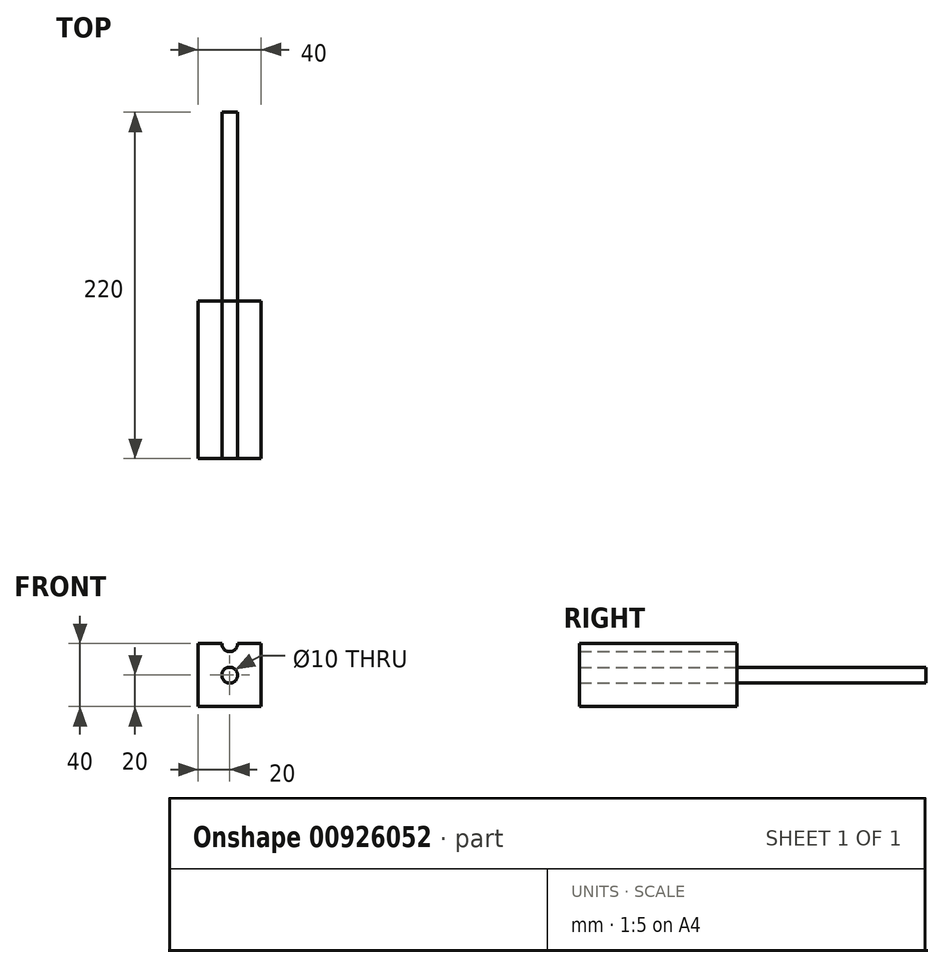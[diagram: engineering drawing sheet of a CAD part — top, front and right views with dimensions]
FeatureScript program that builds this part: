
annotation { "Feature Type Name" : "Feature", "Feature Type Description" : "" }
export const myFeature = defineFeature(function(context is Context, id is Id, definition is map)
    precondition{}
    {
        {
            var Q0;
            Q0=qCreatedBy(makeId("Front.planeOp"),FACE);
            var sketch = newSketch(context, id + "F0", { "sketchPlane" : qUnion([Q0])});
            skLineSegment(sketch, "E0.bottom", {"start": v(-20, 20) * mm, "end": v(-5, 20) * mm});
            skLineSegment(sketch, "E0.top", {"start": v(-20, -20) * mm, "end": v(20, -20) * mm});
            skLineSegment(sketch, "E0.left", {"start": v(-20, 20) * mm, "end": v(-20, -20) * mm});
            skLineSegment(sketch, "E0.right", {"start": v(20, 20) * mm, "end": v(20, -20) * mm});
            skArc(sketch, "E1", {"start": v(-5, 20) * mm, "mid": v(0, 15) * mm, "end": v(5, 20) * mm});
            skLineSegment(sketch, "E2.trimOffspring", {"start": v(5, 20) * mm, "end": v(20, 20) * mm});
            skCircle(sketch, "E3", {"center": v(0, 0) * mm, "radius": 5 * mm});
            skSolve(sketch);
        }
        {
            var Q0;
            Q0 = qSketchRegion(id + "F0", true);
            extrude(context, id + "F1", {"entities" : qUnion([Q0]), "depth" : 100 * mm, "offsetDistance" : 25.4 * mm});
        }
        {
            var Q0;
            Q0=qCreatedBy(makeId("Front.planeOp"),FACE);
            var sketch = newSketch(context, id + "F2", { "sketchPlane" : qUnion([Q0])});
            skCircle(sketch, "E4", {"center": v(0, 0) * mm, "radius": 5 * mm});
            skSolve(sketch);
        }
        {
            var Q0;
            Q0 = qSketchRegion(id + "F2", true);
            extrude(context, id + "F3", {"entities" : qUnion([Q0]), "oppositeDirection" : true, "depth" : 120 * mm, "offsetDistance" : 25.4 * mm});
        }
    });
